annotation { "Feature Type Name" : "Feature", "Feature Type Description" : "" }
export const myFeature = defineFeature(function(context is Context, id is Id, definition is map)
    precondition{}
    {
        {
            var Q0;
            Q0=qCreatedBy(makeId("Front.planeOp"),FACE);
            var sketch = newSketch(context, id + "F0", { "sketchPlane" : qUnion([Q0])});
            skLineSegment(sketch, "E0", {"start": v(0, 0) * mm, "end": v(-4572, 0) * mm});
            skLineSegment(sketch, "E1", {"start": v(0, 0) * mm, "end": v(4572, 0) * mm});
            skLineSegment(sketch, "E2", {"start": v(0, 0) * mm, "end": v(0, 2286) * mm});
            skLineSegment(sketch, "E3", {"start": v(0, 2286) * mm, "end": v(-4572, 0) * mm});
            skLineSegment(sketch, "E4", {"start": v(0, 2286) * mm, "end": v(4572, 0) * mm});
            skLineSegment(sketch, "E5", {"start": v(-4572, 0) * mm, "end": v(-5486.4, 0) * mm});
            skLineSegment(sketch, "E6", {"start": v(-5486.4, 0) * mm, "end": v(0, 2743.2) * mm});
            skLineSegment(sketch, "E7", {"start": v(0, 2743.2) * mm, "end": v(0, 2286) * mm});
            skLineSegment(sketch, "E8", {"start": v(0, 2743.2) * mm, "end": v(5486.4, 0) * mm});
            skLineSegment(sketch, "E9", {"start": v(4572, 0) * mm, "end": v(5486.4, 0) * mm});
            skLineSegment(sketch, "E10", {"start": v(4572, 0) * mm, "end": v(4572, -6705.6) * mm});
            skLineSegment(sketch, "E11", {"start": v(-4572, 0) * mm, "end": v(-4572, -6705.6) * mm});
            skLineSegment(sketch, "E12", {"start": v(-4572, -6705.6) * mm, "end": v(4572, -6705.6) * mm});
            skLineSegment(sketch, "E13", {"start": v(4572, -6705.6) * mm, "end": v(9144, -6705.6) * mm});
            skLineSegment(sketch, "E14", {"start": v(9144, -3352.8) * mm, "end": v(9144, -6705.6) * mm});
            skLineSegment(sketch, "E15", {"start": v(9144, -3352.8) * mm, "end": v(4572, -914.4) * mm});
            skLineSegment(sketch, "E16", {"start": v(4572, -914.4) * mm, "end": v(4572, 0) * mm});
            skLineSegment(sketch, "E17", {"start": v(4572, 0) * mm, "end": v(9144, -2743.2) * mm});
            skLineSegment(sketch, "E18", {"start": v(9144, -2743.2) * mm, "end": v(9144, -3352.8) * mm});
            skLineSegment(sketch, "E19", {"start": v(-4572, -6705.6) * mm, "end": v(-4572, -7315.2) * mm});
            skLineSegment(sketch, "E20", {"start": v(-4572, -7315.2) * mm, "end": v(9144, -7315.2) * mm});
            skLineSegment(sketch, "E21", {"start": v(9144, -7315.2) * mm, "end": v(9144, -6705.6) * mm});
            skLineSegment(sketch, "E22", {"start": v(-4572, -3352.8) * mm, "end": v(4572, -3352.8) * mm, "construction": true});
            skLineSegment(sketch, "E23", {"start": v(-961.62, -6705.6) * mm, "end": v(-961.62, -4572) * mm});
            skLineSegment(sketch, "E24", {"start": v(-961.62, -4572) * mm, "end": v(-47.22, -4572) * mm});
            skLineSegment(sketch, "E25", {"start": v(-47.22, -4572) * mm, "end": v(-47.22, -6705.6) * mm});
            skLineSegment(sketch, "E26.bottom", {"start": v(-3293.04, -2266.15) * mm, "end": v(-1159.44, -2266.15) * mm});
            skLineSegment(sketch, "E26.top", {"start": v(-3293.04, -1351.75) * mm, "end": v(-1159.44, -1351.75) * mm});
            skLineSegment(sketch, "E26.left", {"start": v(-3293.04, -2266.15) * mm, "end": v(-3293.04, -1351.75) * mm});
            skLineSegment(sketch, "E26.right", {"start": v(-1159.44, -2266.15) * mm, "end": v(-1159.44, -1351.75) * mm});
            skLineSegment(sketch, "E27.0", {"start": v(-3445.44, -1199.35) * mm, "end": v(-1007.04, -1199.35) * mm});
            skLineSegment(sketch, "E27.1", {"start": v(-3445.44, -2418.55) * mm, "end": v(-3445.44, -1199.35) * mm});
            skLineSegment(sketch, "E27.2", {"start": v(-3445.44, -2418.55) * mm, "end": v(-1007.04, -2418.55) * mm});
            skLineSegment(sketch, "E27.3", {"start": v(-1007.04, -2418.55) * mm, "end": v(-1007.04, -1199.35) * mm});
            skLineSegment(sketch, "E28.bottom", {"start": v(895.75, -2226.44) * mm, "end": v(3029.35, -2226.44) * mm});
            skLineSegment(sketch, "E28.top", {"start": v(895.75, -1312.04) * mm, "end": v(3029.35, -1312.04) * mm});
            skLineSegment(sketch, "E28.left", {"start": v(895.75, -2226.44) * mm, "end": v(895.75, -1312.04) * mm});
            skLineSegment(sketch, "E28.right", {"start": v(3029.35, -2226.44) * mm, "end": v(3029.35, -1312.04) * mm});
            skLineSegment(sketch, "E29.0", {"start": v(3181.75, -2378.84) * mm, "end": v(3181.75, -1159.64) * mm});
            skLineSegment(sketch, "E29.1", {"start": v(743.35, -2378.84) * mm, "end": v(3181.75, -2378.84) * mm});
            skLineSegment(sketch, "E29.2", {"start": v(743.35, -2378.84) * mm, "end": v(743.35, -1159.64) * mm});
            skLineSegment(sketch, "E29.3", {"start": v(743.35, -1159.64) * mm, "end": v(3181.75, -1159.64) * mm});
            skLineSegment(sketch, "E30.bottom", {"start": v(1114.12, -5700.56) * mm, "end": v(3247.72, -5700.56) * mm});
            skLineSegment(sketch, "E30.top", {"start": v(1114.12, -4786.16) * mm, "end": v(3247.72, -4786.16) * mm});
            skLineSegment(sketch, "E30.left", {"start": v(1114.12, -5700.56) * mm, "end": v(1114.12, -4786.16) * mm});
            skLineSegment(sketch, "E30.right", {"start": v(3247.72, -5700.56) * mm, "end": v(3247.72, -4786.16) * mm});
            skLineSegment(sketch, "E31.0", {"start": v(961.72, -4633.76) * mm, "end": v(3400.12, -4633.76) * mm});
            skLineSegment(sketch, "E31.1", {"start": v(961.72, -5852.96) * mm, "end": v(961.72, -4633.76) * mm});
            skLineSegment(sketch, "E31.2", {"start": v(961.72, -5852.96) * mm, "end": v(3400.12, -5852.96) * mm});
            skLineSegment(sketch, "E31.3", {"start": v(3400.12, -5852.96) * mm, "end": v(3400.12, -4633.76) * mm});
            skSolve(sketch);
        }
        {
            var Q0;
            Q0=makeQuery(id+"F0.imprint","IMPRINT",FACE,{"disambiguationData":[TD([[makeQuery(id+"F0.imprint","IMPRINT",EDGE,{"derivedFrom":sQuery(id+"F0.wireOp",EDGE,"E10")}),1.0]])]});
            var Q1;
            Q1=makeQuery(id+"F0.imprint","IMPRINT",FACE,{"disambiguationData":[TD([[makeQuery(id+"F0.imprint","IMPRINT",EDGE,{"derivedFrom":sQuery(id+"F0.wireOp",EDGE,"E0")}),1.0]])]});
            extrude(context, id + "F1", {"entities" : qUnion([Q0, Q1]), "endBound" : BoundingType.SYMMETRIC, "depth" : 12192 * mm, "offsetDistance" : 30.48 * mm});
        }
        {
            var Q0;
            {var subQ0=sQuery(id+"F0.wireOp",EDGE,"E13");Q0=makeQuery(id+"F0.imprint","IMPRINT",FACE,{"disambiguationData":[TD([[makeQuery(id+"F0.imprint","IMPRINT",EDGE,{"derivedFrom":subQ0}),-1.0]])]});}
            extrude(context, id + "F2", {"entities" : qUnion([Q0]), "endBound" : BoundingType.SYMMETRIC, "depth" : 12496.8 * mm, "offsetDistance" : 30.48 * mm});
        }
        {
            var Q0;
            Q0=makeQuery(id+"F0.imprint","IMPRINT",FACE,{"disambiguationData":[TD([[makeQuery(id+"F0.imprint","IMPRINT",EDGE,{"derivedFrom":sQuery(id+"F0.wireOp",EDGE,"E3")}),-1.0]])]});
            var Q1;
            Q1=makeQuery(id+"F0.imprint","IMPRINT",FACE,{"disambiguationData":[TD([[makeQuery(id+"F0.imprint","IMPRINT",EDGE,{"derivedFrom":sQuery(id+"F0.wireOp",EDGE,"E4")}),1.0]])]});
            var Q2;
            Q2=makeQuery(id+"F0.imprint","IMPRINT",FACE,{"disambiguationData":[TD([[makeQuery(id+"F0.imprint","IMPRINT",EDGE,{"derivedFrom":sQuery(id+"F0.wireOp",EDGE,"E15")}),-1.0]])]});
            extrude(context, id + "F3", {"entities" : qUnion([Q0, Q1, Q2]), "endBound" : BoundingType.SYMMETRIC, "depth" : 12801.6 * mm, "offsetDistance" : 30.48 * mm});
        }
        {
            var Q0;
            Q0=makeQuery(id+"F0.imprint","IMPRINT",FACE,{"disambiguationData":[TD([[makeQuery(id+"F0.imprint","IMPRINT",EDGE,{"derivedFrom":sQuery(id+"F0.wireOp",EDGE,"E0")}),-1.0]])]});
            var Q1;
            Q1=makeQuery(id+"F0.imprint","IMPRINT",FACE,{"disambiguationData":[TD([[makeQuery(id+"F0.imprint","IMPRINT",EDGE,{"derivedFrom":sQuery(id+"F0.wireOp",EDGE,"E1")}),1.0]])]});
            extrude(context, id + "F4", {"entities" : qUnion([Q0, Q1]), "endBound" : BoundingType.SYMMETRIC, "depth" : 12192 * mm, "offsetDistance" : 30.48 * mm});
        }
        {
            var Q0;
            Q0=makeQuery(id+"F0.imprint","IMPRINT",FACE,{"disambiguationData":[TD([[makeQuery(id+"F0.imprint","IMPRINT",EDGE,{"derivedFrom":sQuery(id+"F0.wireOp",EDGE,"E28.bottom")}),1.0]])]});
            var Q1;
            Q1=makeQuery(id+"F0.imprint","IMPRINT",FACE,{"disambiguationData":[TD([[makeQuery(id+"F0.imprint","IMPRINT",EDGE,{"derivedFrom":sQuery(id+"F0.wireOp",EDGE,"E26.bottom")}),1.0]])]});
            var Q2;
            Q2=makeQuery(id+"F0.imprint","IMPRINT",FACE,{"disambiguationData":[TD([[makeQuery(id+"F0.imprint","IMPRINT",EDGE,{"derivedFrom":sQuery(id+"F0.wireOp",EDGE,"E30.bottom")}),1.0]])]});
            extrude(context, id + "F5", {"entities" : qUnion([Q0, Q1, Q2]), "endBound" : BoundingType.SYMMETRIC, "depth" : 11887.2 * mm, "offsetDistance" : 30.48 * mm});
        }
        {
            var Q0;
            Q0=makeQuery(id+"F0.imprint","IMPRINT",FACE,{"disambiguationData":[TD([[makeQuery(id+"F0.imprint","IMPRINT",EDGE,{"derivedFrom":sQuery(id+"F0.wireOp",EDGE,"E30.bottom")}),-1.0]])]});
            var Q1;
            Q1=makeQuery(id+"F0.imprint","IMPRINT",FACE,{"disambiguationData":[TD([[makeQuery(id+"F0.imprint","IMPRINT",EDGE,{"derivedFrom":sQuery(id+"F0.wireOp",EDGE,"E28.bottom")}),-1.0]])]});
            var Q2;
            Q2=makeQuery(id+"F0.imprint","IMPRINT",FACE,{"disambiguationData":[TD([[makeQuery(id+"F0.imprint","IMPRINT",EDGE,{"derivedFrom":sQuery(id+"F0.wireOp",EDGE,"E26.bottom")}),-1.0]])]});
            extrude(context, id + "F6", {"entities" : qUnion([Q0, Q1, Q2]), "endBound" : BoundingType.SYMMETRIC, "depth" : 12192 * mm, "offsetDistance" : 30.48 * mm});
        }
        {
            var Q0;
            Q0=makeQuery(id+"F4.opExtrude","CAP_FACE",FACE,{"disambiguationData":[OSD([sQuery(id+"F0.wireOp",EDGE,"E0"),sQuery(id+"F0.wireOp",EDGE,"E1"),sQuery(id+"F0.wireOp",EDGE,"E3"),sQuery(id+"F0.wireOp",EDGE,"E4")])],"isStart":false});
            var sketch = newSketch(context, id + "F7", { "sketchPlane" : qUnion([Q0])});
            skText(sketch, "E32", { "text": "Owen R.", "fontName": "OpenSans-Regular.ttf"});
            const initialGuessF7  = {"E32": [-1.40738, 0.67685, 1, 0, 0.52479]};
            skSetInitialGuess(sketch, initialGuessF7);
            skSolve(sketch);
        }
        {
            var Q0;
            Q0 = qSketchRegion(id + "F7", true);
            extrude(context, id + "F8", {"entities" : qUnion([Q0]), "operationType" : NewBodyOperationType.ADD, "depth" : 304.8 * mm, "offsetDistance" : 30.48 * mm});
        }
    });